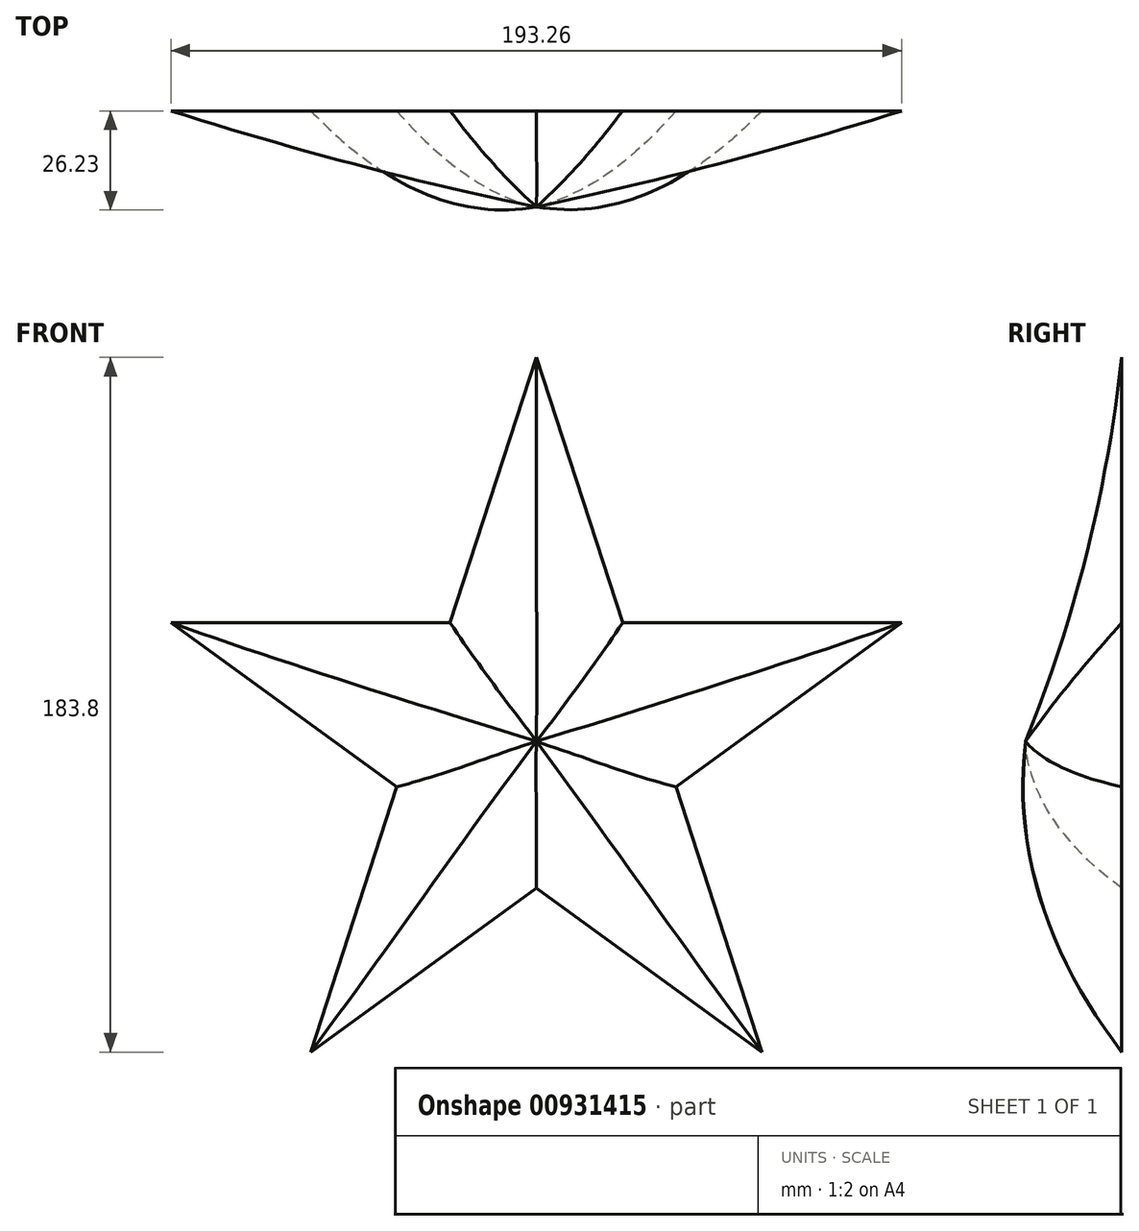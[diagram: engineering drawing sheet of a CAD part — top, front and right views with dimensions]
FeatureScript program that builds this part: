
annotation { "Feature Type Name" : "Feature", "Feature Type Description" : "" }
export const myFeature = defineFeature(function(context is Context, id is Id, definition is map)
    precondition{}
    {
        {
            var Q0;
            Q0=qCreatedBy(makeId("Front.planeOp"),FACE);
            var sketch = newSketch(context, id + "F0", { "sketchPlane" : qUnion([Q0])});
            skCircle(sketch, "E0.cCircle", {"center": v(0, 0) * mm, "radius": 82.2 * mm, "construction": true});
            skLineSegment(sketch, "E0.0", {"start": v(96.63, 31.4) * mm, "end": v(59.72, -82.2) * mm});
            skLineSegment(sketch, "E0.1", {"start": v(59.72, -82.2) * mm, "end": v(-59.72, -82.2) * mm});
            skLineSegment(sketch, "E0.2", {"start": v(-59.72, -82.2) * mm, "end": v(-96.63, 31.4) * mm});
            skLineSegment(sketch, "E0.3", {"start": v(-96.63, 31.4) * mm, "end": v(0, 101.6) * mm});
            skLineSegment(sketch, "E0.4", {"start": v(0, 101.6) * mm, "end": v(96.63, 31.4) * mm});
            skPoint(sketch, "E0.0.midPoint", {"position": v(78.17, -25.4) * mm});
            skLineSegment(sketch, "E1", {"start": v(0, 101.6) * mm, "end": v(-59.72, -82.2) * mm});
            skLineSegment(sketch, "E2", {"start": v(-59.72, -82.2) * mm, "end": v(96.63, 31.4) * mm});
            skLineSegment(sketch, "E3", {"start": v(96.63, 31.4) * mm, "end": v(-96.63, 31.4) * mm});
            skLineSegment(sketch, "E4", {"start": v(59.72, -82.2) * mm, "end": v(-96.63, 31.4) * mm});
            skLineSegment(sketch, "E5", {"start": v(0, 101.6) * mm, "end": v(59.72, -82.2) * mm});
            skSolve(sketch);
        }
        {
            var Q0;
            Q0=qCreatedBy(makeId("Front.planeOp"),FACE);
            var sketch = newSketch(context, id + "F1", { "sketchPlane" : qUnion([Q0])});
            skLineSegment(sketch, "E6.0", {"start": v(0, 101.6) * mm, "end": v(-22.81, 31.4) * mm});
            skLineSegment(sketch, "E7.0", {"start": v(0, 101.6) * mm, "end": v(22.81, 31.4) * mm});
            skLineSegment(sketch, "E8.0", {"start": v(96.63, 31.4) * mm, "end": v(22.81, 31.4) * mm});
            skLineSegment(sketch, "E9.0", {"start": v(59.72, -82.2) * mm, "end": v(0, -38.8) * mm});
            skLineSegment(sketch, "E10.0", {"start": v(-59.72, -82.2) * mm, "end": v(0, -38.8) * mm});
            skLineSegment(sketch, "E11.trimOffspring", {"start": v(36.9, -12) * mm, "end": v(59.72, -82.2) * mm});
            skLineSegment(sketch, "E12.trimOffspring", {"start": v(-22.81, 31.4) * mm, "end": v(-96.63, 31.4) * mm});
            skLineSegment(sketch, "E13.trimOffspring", {"start": v(-36.9, -12) * mm, "end": v(-59.72, -82.2) * mm});
            skLineSegment(sketch, "E14.trimOffspring", {"start": v(-36.9, -12) * mm, "end": v(-96.63, 31.4) * mm});
            skLineSegment(sketch, "E15.trimOffspring", {"start": v(36.9, -12) * mm, "end": v(96.63, 31.4) * mm});
            skSolve(sketch);
        }
        {
            var Q0;
            Q0=qCreatedBy(makeId("Front.planeOp"),FACE);
            cPlane(context, id + "F2", {"entities" : qUnion([Q0]), "cplaneType" : CPlaneType.OFFSET, "offset" : 25.4 * mm, "width" : 152.4 * mm, "height" : 152.4 * mm});
        }
        {
            var Q0;
            Q0=qCreatedBy(id+"F2.planeOp",FACE);
            var sketch = newSketch(context, id + "F3", { "sketchPlane" : qUnion([Q0])});
            skPoint(sketch, "E16.0", {"position": v(0, 0) * mm});
            skSolve(sketch);
        }
        {
            var Q0;
            Q0=qCreatedBy(makeId("Right.planeOp"),FACE);
            var sketch = newSketch(context, id + "F4", { "sketchPlane" : qUnion([Q0])});
            skPoint(sketch, "E17.0", {"position": v(0, 101.6) * mm});
            skPoint(sketch, "E18.0", {"position": v(-25.4, 0) * mm});
            skArc(sketch, "E19", {"start": v(-25.4, 0) * mm, "mid": v(-9.25, 49.94) * mm, "end": v(0, 101.6) * mm});
            skSolve(sketch);
        }
        {
            var Q0;
            Q0=sQuery(id+"F4.wireOp",EDGE,"E19");
            var Q1;
            Q1=makeQuery(id+"F1.imprint","IMPRINT",FACE,{"disambiguationData":[TD([[makeQuery(id+"F1.imprint","IMPRINT",EDGE,{"derivedFrom":sQuery(id+"F1.wireOp",EDGE,"E6.0")}),1.0]])]});
            var Q2;
            Q2=sQuery(id+"F3.wireOp",VERTEX,"E16.0");
            var Q3;
            Q3=makeQuery(id+"F1.imprint","IMPRINT",FACE,{"disambiguationData":[TD([[makeQuery(id+"F1.imprint","IMPRINT",EDGE,{"derivedFrom":sQuery(id+"F1.wireOp",EDGE,"E6.0")}),1.0]])]});
            var Q4;
            Q4=sQuery(id+"F3.wireOp",VERTEX,"E16.0");
            var Q5;
            Q5=sQuery(id+"F4.wireOp",EDGE,"E19");
            loft(context, id + "F5", {"bodyType" : ToolBodyType.SURFACE, "addSections" : true, "spine" : qUnion([Q0]), "sectionCount" : 7, "sheetProfilesArray" : [{ "sheetProfileEntities" : qUnion([Q1]) }, { "sheetProfileEntities" : qUnion([Q2]) }], "wireProfilesArray" : [{ "wireProfileEntities" : qUnion([Q3]) }, { "wireProfileEntities" : qUnion([Q4]) }], "guidesArray" : [{ "guideEntities" : qUnion([Q5]), "guideDerivativeType" : LoftGuideDerivativeType.DEFAULT, "guideDerivativeMagnitude" : 1 }]});
        }
    });
